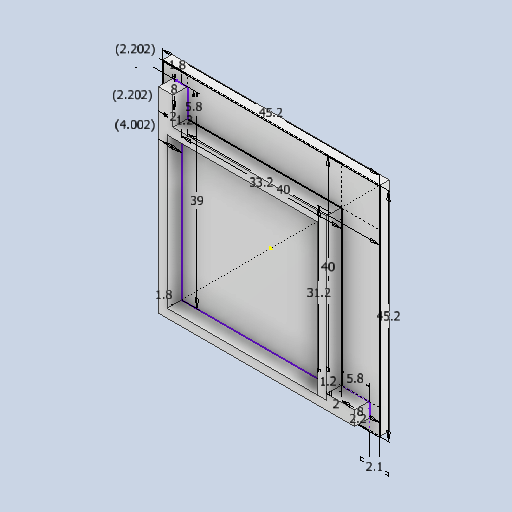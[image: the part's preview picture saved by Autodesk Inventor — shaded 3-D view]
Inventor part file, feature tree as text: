
AUTODESK INVENTOR PART (.ipt)
format: ipt  version: 2023 (Build 270158000, 158)  size: 303,616 bytes
history: native  units: in
note: dims shown in document units (in); Inventor stores cm internally (conversion verified against a paired STEP export)
features: extrude x4, sketch x1, fillet x1
ambient origin geometry x8: Origin, YZ Plane, XZ Plane, XY Plane, X Axis, Y Axis, Z Axis, Center Point
bodies: Solid1 (feature_tree)
feature tree (6):
  sketch  "Sketch1"  dims[d0=1.7795in d1=1.7795in d2=0.0827in d3=0.0866in d5=0.0709in d6=0.0709in d7=1.5354in d8=0.1181in d9=0.0in d10=0.0867in d11=0.1576in d12=0.0867in d13=0.0787in d14=0.0in d15=0.0472in d16=0.2283in d21=0.2283in d22=0.0472in d23=0.1181in d24=0.0in d25=1.5748in d26=0.315in d27=0.315in d28=1.5748in d29=1.3071in d30=0.0787in d31=0.0787in d32=1.2283in d33=0.1181in d34=0.0in d35=0.0394in]
  extrude  "Extrusion1"  Depth=1.7795in
  extrude  "Extrusion2"  Depth=0.0394in
  extrude  "Extrusion4"  Depth=0.0394in
  extrude  "Extrusion5"  Depth=0.0709in
  fillet  "Fillet1"  Radius=0.0709in
